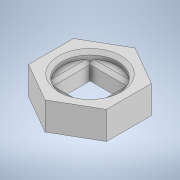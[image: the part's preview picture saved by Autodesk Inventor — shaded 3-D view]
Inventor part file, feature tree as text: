
AUTODESK INVENTOR PART (.ipt)
format: ipt  version: 2022 (Build 260153000, 153)  size: 134,144 bytes
history: native  units: in
note: dims shown in document units (in); Inventor stores cm internally (conversion verified against a paired STEP export)
features: extrude x2, chamfer x2, sketch x2
ambient origin geometry x8: Origin, YZ Plane, XZ Plane, XY Plane, X Axis, Y Axis, Z Axis, Center Point
bodies: Solid1 (feature_tree)
feature tree (6):
  extrude  "Extrusion1"  Depth=0.261in
  extrude  "Extrusion2"  Depth=0.05in
  chamfer  "Chamfer1"  Distance=0.05in
  chamfer  "Chamfer2"  Distance=0.0236in Angle=45.0deg
  sketch  "Sketch1"  dims[d0=0.5512in d1=0.261in]
  sketch  "Sketch2"  dims[d2=0.1969in d3=0.0in d4=0.3957in d5=0.05in d6=0.0in d7=0.0236in d8=0.125in d9=45.0deg d10=0.0236in d11=0.125in d12=45.0deg]
